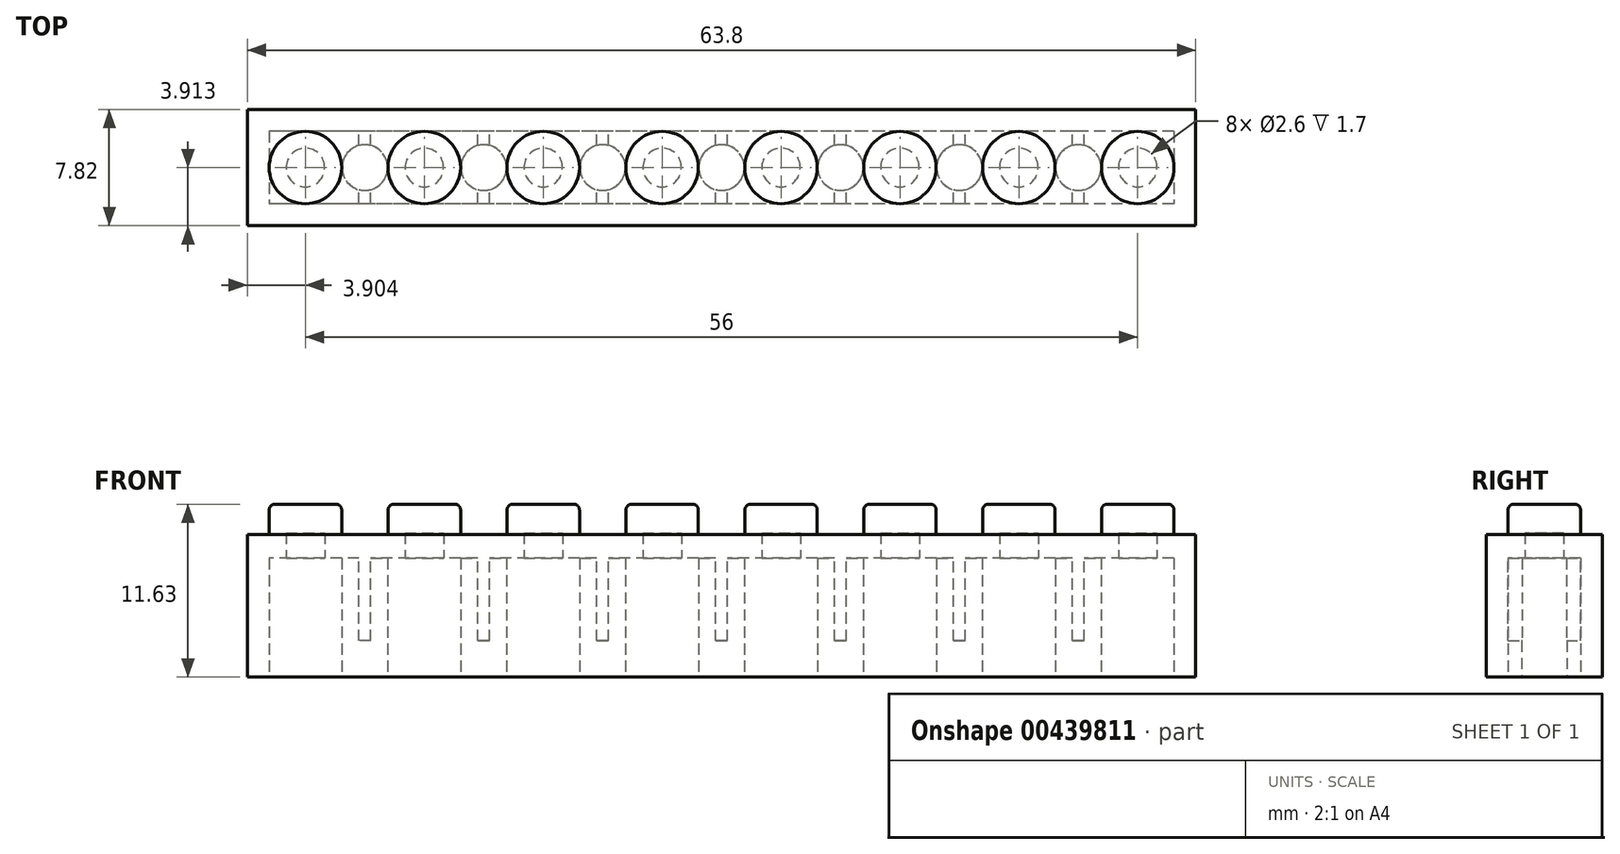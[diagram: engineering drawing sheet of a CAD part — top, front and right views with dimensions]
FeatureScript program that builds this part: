
annotation { "Feature Type Name" : "Feature", "Feature Type Description" : "" }
export const myFeature = defineFeature(function(context is Context, id is Id, definition is map)
    precondition{}
    {
        {
            var Q0;
            Q0=qCreatedBy(makeId("Top.planeOp"),FACE);
            var sketch = newSketch(context, id + "F0", { "sketchPlane" : qUnion([Q0])});
            skLineSegment(sketch, "E0.bottom", {"start": v(-34.24, -11.37) * mm, "end": v(29.56, -11.37) * mm});
            skLineSegment(sketch, "E0.top", {"start": v(-34.24, -19.19) * mm, "end": v(29.56, -19.19) * mm});
            skLineSegment(sketch, "E0.left", {"start": v(-34.24, -11.37) * mm, "end": v(-34.24, -19.19) * mm});
            skLineSegment(sketch, "E0.right", {"start": v(29.56, -11.37) * mm, "end": v(29.56, -19.19) * mm});
            skSolve(sketch);
        }
        {
            var Q0;
            Q0 = qSketchRegion(id + "F0", true);
            extrude(context, id + "F1", {"entities" : qUnion([Q0]), "depth" : 9.6 * mm});
        }
        {
            var Q0;
            Q0=makeQuery(id+"F1.opExtrude","CAP_FACE",FACE,{"disambiguationData":[OSD([sQuery(id+"F0.wireOp",EDGE,"E0.bottom"),sQuery(id+"F0.wireOp",EDGE,"E0.top"),sQuery(id+"F0.wireOp",EDGE,"E0.left"),sQuery(id+"F0.wireOp",EDGE,"E0.right")])],"isStart":false});
            var sketch = newSketch(context, id + "F2", { "sketchPlane" : qUnion([Q0])});
            skCircle(sketch, "E1", {"center": v(-30.34, -15.28) * mm, "radius": 2.44 * mm});
            skLineSegment(sketch, "E2", {"start": v(-34.24, -15.28) * mm, "end": v(29.56, -15.28) * mm, "construction": true});
            skLineSegment(sketch, "E3", {"start": v(-2.34, -11.37) * mm, "end": v(-2.34, -19.19) * mm, "construction": true});
            skCircle(sketch, "E4.1.0.0", {"center": v(-22.34, -15.28) * mm, "radius": 2.44 * mm});
            skCircle(sketch, "E4.2.0.0", {"center": v(-14.34, -15.28) * mm, "radius": 2.44 * mm});
            skCircle(sketch, "E4.3.0.0", {"center": v(-6.34, -15.28) * mm, "radius": 2.44 * mm});
            skCircle(sketch, "E4.4.0.0", {"center": v(1.66, -15.28) * mm, "radius": 2.44 * mm});
            skCircle(sketch, "E4.5.0.0", {"center": v(9.66, -15.28) * mm, "radius": 2.44 * mm});
            skCircle(sketch, "E4.6.0.0", {"center": v(17.66, -15.28) * mm, "radius": 2.44 * mm});
            skCircle(sketch, "E4.7.0.0", {"center": v(25.66, -15.28) * mm, "radius": 2.44 * mm});
            skLineSegment(sketch, "E4.direction1", {"start": v(-30.34, -15.28) * mm, "end": v(-22.34, -15.28) * mm, "construction": true});
            skSolve(sketch);
        }
        {
            var Q0;
            Q0 = qSketchRegion(id + "F2", true);
            extrude(context, id + "F3", {"entities" : qUnion([Q0]), "operationType" : NewBodyOperationType.ADD, "depth" : 2.03 * mm});
        }
        {
            var Q0;
            Q0=makeQuery(id+"F1.opExtrude","CAP_FACE",FACE,{"disambiguationData":[OSD([sQuery(id+"F0.wireOp",EDGE,"E0.bottom"),sQuery(id+"F0.wireOp",EDGE,"E0.top"),sQuery(id+"F0.wireOp",EDGE,"E0.left"),sQuery(id+"F0.wireOp",EDGE,"E0.right")])],"isStart":true});
            var sketch = newSketch(context, id + "F4", { "sketchPlane" : qUnion([Q0])});
            skLineSegment(sketch, "E5.bottom", {"start": v(28.1, 12.84) * mm, "end": v(-32.76, 12.84) * mm});
            skLineSegment(sketch, "E5.top", {"start": v(28.1, 17.72) * mm, "end": v(-32.76, 17.72) * mm});
            skLineSegment(sketch, "E5.left", {"start": v(28.1, 12.84) * mm, "end": v(28.1, 17.72) * mm});
            skLineSegment(sketch, "E5.right", {"start": v(-32.76, 12.84) * mm, "end": v(-32.76, 17.72) * mm});
            skLineSegment(sketch, "E6", {"start": v(-34.24, 15.28) * mm, "end": v(29.56, 15.28) * mm, "construction": true});
            skLineSegment(sketch, "E7", {"start": v(-2.34, 19.19) * mm, "end": v(-2.34, 11.37) * mm, "construction": true});
            skCircle(sketch, "E8", {"center": v(-26.34, 15.28) * mm, "radius": 1.54 * mm});
            skCircle(sketch, "E9.1.0.0", {"center": v(-18.34, 15.28) * mm, "radius": 1.54 * mm});
            skLineSegment(sketch, "E9.1.0.1", {"start": v(-26.24, 15.28) * mm, "end": v(37.56, 15.28) * mm, "construction": true});
            skCircle(sketch, "E9.2.0.0", {"center": v(-10.34, 15.28) * mm, "radius": 1.54 * mm});
            skLineSegment(sketch, "E9.2.0.1", {"start": v(-18.24, 15.28) * mm, "end": v(45.56, 15.28) * mm, "construction": true});
            skLineSegment(sketch, "E9.direction1", {"start": v(-26.34, 15.28) * mm, "end": v(-18.34, 15.28) * mm, "construction": true});
            skCircle(sketch, "E10.0.3.0", {"center": v(-2.34, 15.28) * mm, "radius": 1.54 * mm});
            skLineSegment(sketch, "E10.2.3.0", {"start": v(-10.24, 15.28) * mm, "end": v(53.56, 15.28) * mm, "construction": true});
            skCircle(sketch, "E10.0.4.0", {"center": v(5.66, 15.28) * mm, "radius": 1.54 * mm});
            skLineSegment(sketch, "E10.2.4.0", {"start": v(-2.24, 15.28) * mm, "end": v(61.56, 15.28) * mm, "construction": true});
            skCircle(sketch, "E10.0.5.0", {"center": v(13.66, 15.28) * mm, "radius": 1.54 * mm});
            skLineSegment(sketch, "E10.2.5.0", {"start": v(5.76, 15.28) * mm, "end": v(69.56, 15.28) * mm, "construction": true});
            skCircle(sketch, "E10.0.6.0", {"center": v(21.66, 15.28) * mm, "radius": 1.54 * mm});
            skLineSegment(sketch, "E10.2.6.0", {"start": v(13.76, 15.28) * mm, "end": v(77.56, 15.28) * mm, "construction": true});
            skSolve(sketch);
        }
        {
            var Q0;
            Q0 = qSketchRegion(id + "F4", true);
            extrude(context, id + "F5", {"entities" : qUnion([Q0]), "operationType" : NewBodyOperationType.REMOVE, "oppositeDirection" : true, "depth" : (9.6 - 1.6) * mm});
        }
        {
            var Q0;
            Q0=makeQuery(id+"F3.opExtrude","CAP_EDGE",EDGE,{"disambiguationData":[OSD([sQuery(id+"F2.wireOp",EDGE,"E4.1.0.0")])],"isStart":false});
            var Q1;
            Q1=makeQuery(id+"F3.opExtrude","CAP_EDGE",EDGE,{"disambiguationData":[OSD([sQuery(id+"F2.wireOp",EDGE,"E4.2.0.0")])],"isStart":false});
            var Q2;
            Q2=makeQuery(id+"F3.opExtrude","CAP_EDGE",EDGE,{"disambiguationData":[OSD([sQuery(id+"F2.wireOp",EDGE,"E4.3.0.0")])],"isStart":false});
            var Q3;
            Q3=makeQuery(id+"F3.opExtrude","CAP_EDGE",EDGE,{"disambiguationData":[OSD([sQuery(id+"F2.wireOp",EDGE,"E4.4.0.0")])],"isStart":false});
            var Q4;
            Q4=makeQuery(id+"F3.opExtrude","CAP_EDGE",EDGE,{"disambiguationData":[OSD([sQuery(id+"F2.wireOp",EDGE,"E4.5.0.0")])],"isStart":false});
            var Q5;
            Q5=makeQuery(id+"F3.opExtrude","CAP_EDGE",EDGE,{"disambiguationData":[OSD([sQuery(id+"F2.wireOp",EDGE,"E4.6.0.0")])],"isStart":false});
            var Q6;
            Q6=makeQuery(id+"F3.opExtrude","CAP_EDGE",EDGE,{"disambiguationData":[OSD([sQuery(id+"F2.wireOp",EDGE,"E4.7.0.0")])],"isStart":false});
            var Q7;
            Q7=makeQuery(id+"F3.opExtrude","CAP_EDGE",EDGE,{"disambiguationData":[OSD([sQuery(id+"F2.wireOp",EDGE,"E1")])],"isStart":false});
            fillet(context, id + "F6", {"entities" : qUnion([Q0, Q1, Q2, Q3, Q4, Q5, Q6, Q7]), "radius" : 0.38 * mm, "tangentPropagation" : true, "allowEdgeOverflow" : false});
        }
        {
            var Q0;
            Q0=makeQuery(id+"F5.boolean.opBoolean","COPY",FACE,{"derivedFrom":makeQuery(id+"F5.opExtrude","CAP_FACE",FACE,{"disambiguationData":[OSD([sQuery(id+"F4.wireOp",EDGE,"E5.bottom"),sQuery(id+"F4.wireOp",EDGE,"E5.top"),sQuery(id+"F4.wireOp",EDGE,"E5.left"),sQuery(id+"F4.wireOp",EDGE,"E5.right"),sQuery(id+"F4.wireOp",EDGE,"E8"),sQuery(id+"F4.wireOp",EDGE,"E9.1.0.0"),sQuery(id+"F4.wireOp",EDGE,"E9.2.0.0"),sQuery(id+"F4.wireOp",EDGE,"E10.0.3.0"),sQuery(id+"F4.wireOp",EDGE,"E10.0.4.0"),sQuery(id+"F4.wireOp",EDGE,"E10.0.5.0"),sQuery(id+"F4.wireOp",EDGE,"E10.0.6.0")])],"isStart":false})});
            var sketch = newSketch(context, id + "F7", { "sketchPlane" : qUnion([Q0])});
            skLineSegment(sketch, "E11.bottom", {"start": v(-26.74, 17.72) * mm, "end": v(-25.94, 17.72) * mm});
            skLineSegment(sketch, "E11.top", {"start": v(-26.74, 12.84) * mm, "end": v(-25.94, 12.84) * mm});
            skLineSegment(sketch, "E11.left", {"start": v(-26.74, 17.72) * mm, "end": v(-26.74, 12.84) * mm});
            skLineSegment(sketch, "E11.right", {"start": v(-25.94, 17.72) * mm, "end": v(-25.94, 12.84) * mm});
            skPoint(sketch, "E11.middle", {"position": v(-26.34, 15.28) * mm});
            skLineSegment(sketch, "E12.1.0.0", {"start": v(-18.74, 17.72) * mm, "end": v(-17.94, 17.72) * mm});
            skLineSegment(sketch, "E12.1.0.1", {"start": v(-18.74, 17.72) * mm, "end": v(-18.74, 12.84) * mm});
            skLineSegment(sketch, "E12.1.0.2", {"start": v(-18.74, 12.84) * mm, "end": v(-17.94, 12.84) * mm});
            skLineSegment(sketch, "E12.1.0.3", {"start": v(-17.94, 17.72) * mm, "end": v(-17.94, 12.84) * mm});
            skLineSegment(sketch, "E12.2.0.0", {"start": v(-10.74, 17.72) * mm, "end": v(-9.94, 17.72) * mm});
            skLineSegment(sketch, "E12.2.0.1", {"start": v(-10.74, 17.72) * mm, "end": v(-10.74, 12.84) * mm});
            skLineSegment(sketch, "E12.2.0.2", {"start": v(-10.74, 12.84) * mm, "end": v(-9.94, 12.84) * mm});
            skLineSegment(sketch, "E12.2.0.3", {"start": v(-9.94, 17.72) * mm, "end": v(-9.94, 12.84) * mm});
            skLineSegment(sketch, "E12.3.0.0", {"start": v(-2.74, 17.72) * mm, "end": v(-1.94, 17.72) * mm});
            skLineSegment(sketch, "E12.3.0.1", {"start": v(-2.74, 17.72) * mm, "end": v(-2.74, 12.84) * mm});
            skLineSegment(sketch, "E12.3.0.2", {"start": v(-2.74, 12.84) * mm, "end": v(-1.94, 12.84) * mm});
            skLineSegment(sketch, "E12.3.0.3", {"start": v(-1.94, 17.72) * mm, "end": v(-1.94, 12.84) * mm});
            skLineSegment(sketch, "E12.4.0.0", {"start": v(5.26, 17.72) * mm, "end": v(6.06, 17.72) * mm});
            skLineSegment(sketch, "E12.4.0.1", {"start": v(5.26, 17.72) * mm, "end": v(5.26, 12.84) * mm});
            skLineSegment(sketch, "E12.4.0.2", {"start": v(5.26, 12.84) * mm, "end": v(6.06, 12.84) * mm});
            skLineSegment(sketch, "E12.4.0.3", {"start": v(6.06, 17.72) * mm, "end": v(6.06, 12.84) * mm});
            skLineSegment(sketch, "E12.5.0.0", {"start": v(13.26, 17.72) * mm, "end": v(14.06, 17.72) * mm});
            skLineSegment(sketch, "E12.5.0.1", {"start": v(13.26, 17.72) * mm, "end": v(13.26, 12.84) * mm});
            skLineSegment(sketch, "E12.5.0.2", {"start": v(13.26, 12.84) * mm, "end": v(14.06, 12.84) * mm});
            skLineSegment(sketch, "E12.5.0.3", {"start": v(14.06, 17.72) * mm, "end": v(14.06, 12.84) * mm});
            skLineSegment(sketch, "E12.6.0.0", {"start": v(21.26, 17.72) * mm, "end": v(22.06, 17.72) * mm});
            skLineSegment(sketch, "E12.6.0.1", {"start": v(21.26, 17.72) * mm, "end": v(21.26, 12.84) * mm});
            skLineSegment(sketch, "E12.6.0.2", {"start": v(21.26, 12.84) * mm, "end": v(22.06, 12.84) * mm});
            skLineSegment(sketch, "E12.6.0.3", {"start": v(22.06, 17.72) * mm, "end": v(22.06, 12.84) * mm});
            skLineSegment(sketch, "E12.direction1", {"start": v(-26.74, 12.84) * mm, "end": v(-18.74, 12.84) * mm, "construction": true});
            skSolve(sketch);
        }
        {
            var Q0;
            Q0 = qSketchRegion(id + "F7", true);
            extrude(context, id + "F8", {"entities" : qUnion([Q0]), "operationType" : NewBodyOperationType.ADD, "depth" : 8 * mm - 2.44 * mm});
        }
        {
            var Q0;
            {var subQ0=sQuery(id+"F4.wireOp",EDGE,"E5.right");var subQ1=sQuery(id+"F4.wireOp",EDGE,"E5.top");var subQ2=sQuery(id+"F4.wireOp",EDGE,"E8");var subQ3=sQuery(id+"F4.wireOp",EDGE,"E5.bottom");var subQ4=sQuery(id+"F4.wireOp",EDGE,"E9.1.0.0");Q0=makeQuery(id+"F8.boolean.opBoolean","SPLIT",FACE,{"disambiguationData":[TD([makeQuery(id+"F5.boolean.opBoolean","COPY",FACE,{"derivedFrom":makeQuery(id+"F5.opExtrude","SWEPT_FACE",FACE,{"disambiguationData":[OSD([subQ0])]})})])],"derivedFrom":makeQuery(id+"F5.boolean.opBoolean","COPY",FACE,{"derivedFrom":makeQuery(id+"F5.opExtrude","CAP_FACE",FACE,{"disambiguationData":[OSD([subQ3,subQ1,sQuery(id+"F4.wireOp",EDGE,"E5.left"),subQ0,subQ2,subQ4,sQuery(id+"F4.wireOp",EDGE,"E9.2.0.0"),sQuery(id+"F4.wireOp",EDGE,"E10.0.3.0"),sQuery(id+"F4.wireOp",EDGE,"E10.0.4.0"),sQuery(id+"F4.wireOp",EDGE,"E10.0.5.0"),sQuery(id+"F4.wireOp",EDGE,"E10.0.6.0")])],"isStart":false})})});}
            var sketch = newSketch(context, id + "F9", { "sketchPlane" : qUnion([Q0])});
            skCircle(sketch, "E13", {"center": v(-30.34, 15.28) * mm, "radius": 1.3 * mm});
            skCircle(sketch, "E14.1.0.0", {"center": v(-22.34, 15.28) * mm, "radius": 1.3 * mm});
            skCircle(sketch, "E14.2.0.0", {"center": v(-14.34, 15.28) * mm, "radius": 1.3 * mm});
            skCircle(sketch, "E14.3.0.0", {"center": v(-6.34, 15.28) * mm, "radius": 1.3 * mm});
            skCircle(sketch, "E14.4.0.0", {"center": v(1.66, 15.28) * mm, "radius": 1.3 * mm});
            skCircle(sketch, "E14.5.0.0", {"center": v(9.66, 15.28) * mm, "radius": 1.3 * mm});
            skCircle(sketch, "E14.6.0.0", {"center": v(17.66, 15.28) * mm, "radius": 1.3 * mm});
            skLineSegment(sketch, "E14.direction1", {"start": v(-30.34, 15.28) * mm, "end": v(-22.34, 15.28) * mm, "construction": true});
            skCircle(sketch, "E15.0.7.0", {"center": v(25.66, 15.28) * mm, "radius": 1.3 * mm});
            skSolve(sketch);
        }
        {
            var Q0;
            Q0 = qSketchRegion(id + "F9", true);
            extrude(context, id + "F10", {"entities" : qUnion([Q0]), "operationType" : NewBodyOperationType.REMOVE, "oppositeDirection" : true, "depth" : 1.7 * mm});
        }
    });
